# Revit family: Fire-Products_Sprinkler-Systems_YAMATO-PROTEC_YMT2
name_source: partatom
category: スプリンクラ
revit_build: Autodesk Revit 2018 (Build: 20170223_1515(x64)
units: mm (PartAtom-declared; Revit-internal decimal feet)

## family parameters
OmniClass タイトル = Water Fire Fighting Terminals
OmniClass 番号 = 23.65.70.17.14
パーツ タイプ = 標準
ロード時にボイドで切り取り = はい
丸型コネクタ寸法 = 直径を使用
作業面ベース = いいえ
共有 = いいえ
常に垂直 = はい
注釈の向きを維持 = いいえ
部屋計算ポイント = いいえ

## types (1)
- YMT2
    Depth = 74  [stored 0.242782 ft]
    Height = 156  [stored 0.511811 ft]
    IfcExportAs = IfcFireSuppressionTerminalType
    IfcExportType = SPRINKLER
    OmniClassCode = 23-29 25 11 13
    ProductInformation = https://www.yamatoprotec.co.jp
    URL = https://www.yamatoprotec.co.jp
    Uniclass2015Code = Pr_65_54_30_23
    Uniclass2015Title = Drain and test valves
    Uniclass2015Version = Systems v1.9
    Width = 282
    モデル = YMT2
    仕様書バージョン = Version1.0
    企業コード = 580077214
    入口径 = 25.00 mm
    分類コード = 50903001200000
    呼称 = 末端試験装置
    最高使用圧力 = 1.4 MPa
    積算_科目 = 9 消火設備
    製品リリース年月 = 2010年3月
    製造元 = ヤマトプロテック株式会社
    説明 = 末端試験装置 YMT2
    質量 = 15.00 kg

note: [stored X ft] marks values corroborated as IEEE doubles in the binary element streams (Revit-internal decimal feet)
